# Revit family: Sanitary_Taps-Mixers_TOTO-USA-Inc_Helix-M-EcoPower-Faucet-0-5-GPM
name_source: partatom
category: Plumbing Fixtures
revit_build: Autodesk Revit 2015 (Build: 20140606_1530(x64)
units: mm (PartAtom-declared; Revit-internal decimal feet)

## types (1)
- TELS125
    BIMobject category = Taps & Mixers
    BIMobject category code = sanitary-taps-mixers
    BIMobject main category = Sanitary
    BIMobject main category code = sanitary
    Brand url = https://www.totousa.com
    Default Elevation = 4' - 0"
    Description = Beautifully designed for high traffic spaces, the Helix EcoPower Faucet harnesses the energy of running water to power itself. The intuitive Smart Sensor technology accurately detects the user for rapid water disbursement.
    Edition number = 1
    Humidity = Max. 90% RH
    IFC Classification = Sanitary Terminal
    Installation instructions = https://www.totousa.com
    Manufacturer = TOTO
    Manufacturer name = TOTO USA Inc
    Masterformat 2014 Code = 10 28 00
    Masterformat 2014 Description = Toilet, Bath, and Laundry Accessories
    Material = Metal - TOTO - Stainless Steel
    Material main = Polished Chrome
    Model = TELS125
    NBS Reference Code = 35-06-07
    NBS Reference Description = Bath Water Supply Fittings
    Nominal height = 0' - 0"
    Nominal width = 0' - 0"
    OmniClass Code = 23-31 11 00
    OmniClass Description = Faucets
    Product Guid = a5606b2f-feff-4fd9-b337-6f3df5532b4f
    Product SKU = toto-tel125-d10e
    Product certification = https://www.totousa.com
    Product data url = https://bimobject.com
    Product family = Single Faucets
    Product group = Helix??
    Product url = https://www.totousa.com
    QR code = http://bimobject.com
    Sensor Detection Range = 5-1/8" - 7-7/8" (130 - 200mm)
    Technical description = https://www.totousa.com
    UNSPSC Code = 30181505
    Uniclass 1.4 Code = L725111
    Uniclass 1.4 Description = Mixer taps
    Uniclass 2.0 Code = PR-35-06-07
    Uniclass 2.0 Description = Bath Water Supply Fittings
    Uniclass 2015 Code = Pr_40_20_87_84
    Uniclass 2015 Name = Sink taps
    Uniformat II Code = D2030
    Uniformat II Description = Sanitary Waste
    Warranty = Three years
    Water Supply Connection = 0' - 0 1/2"
    Youtube clip = https://youtu.be

## geometry (parser evidence)
native form markers: Blend x4, Sweep x2
no freeform markers — native parametric forms only
